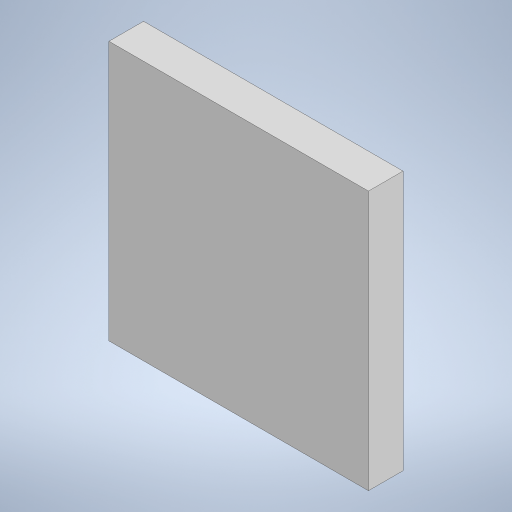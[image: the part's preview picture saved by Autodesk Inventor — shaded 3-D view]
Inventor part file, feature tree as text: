
AUTODESK INVENTOR PART (.ipt)
format: ipt  version: 2023 (Build 270158000, 158)  size: 186,880 bytes
history: native  units: in
note: dims shown in document units (in); Inventor stores cm internally (conversion verified against a paired STEP export)
features: extrude x1, sketch x1
ambient origin geometry x8: Origin, YZ Plane, XZ Plane, XY Plane, X Axis, Y Axis, Z Axis, Center Point
bodies: Solid1 (feature_tree)
feature tree (2):
  extrude  "Extrusion1"  Depth=0.5906in
  sketch  "Sketch1"  dims[d0=0.5906in d1=0.5906in d2=0.0787in d3=0.0in]
